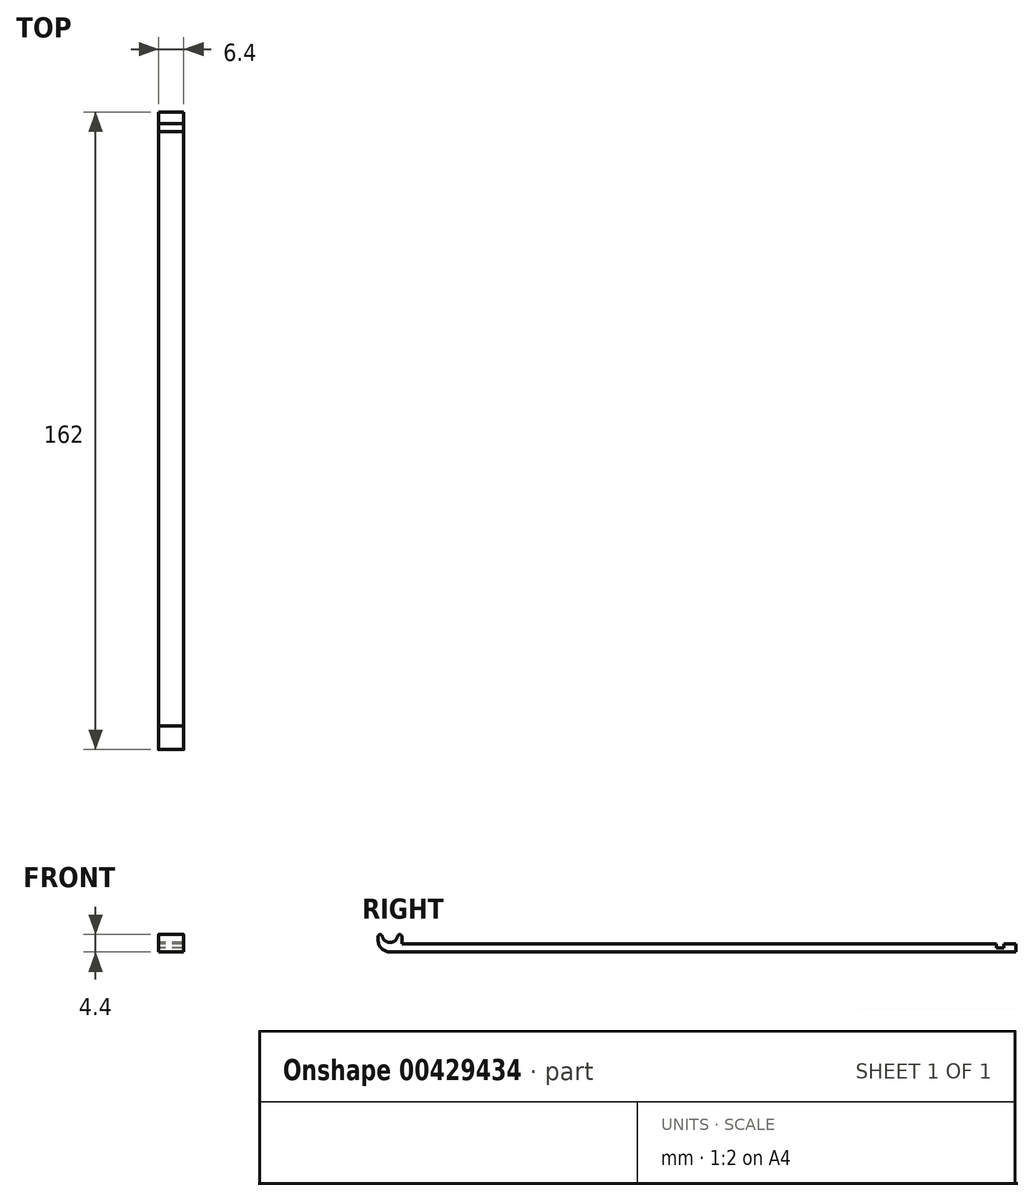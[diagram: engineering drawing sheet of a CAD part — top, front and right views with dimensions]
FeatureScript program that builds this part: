
annotation { "Feature Type Name" : "Feature", "Feature Type Description" : "" }
export const myFeature = defineFeature(function(context is Context, id is Id, definition is map)
    precondition{}
    {
        {
            var Q0;
            Q0=qCreatedBy(makeId("Right.planeOp"),FACE);
            var sketch = newSketch(context, id + "F0", { "sketchPlane" : qUnion([Q0])});
            skLineSegment(sketch, "E0.bottom", {"start": v(0, 0) * mm, "end": v(-159, 0) * mm});
            skLineSegment(sketch, "E0.top", {"start": v(0, 2) * mm, "end": v(-156, 2) * mm});
            skLineSegment(sketch, "E0.left", {"start": v(0, 0) * mm, "end": v(0, 2) * mm});
            skArc(sketch, "E1", {"start": v(-160.96, 4) * mm, "mid": v(-159, 2.4) * mm, "end": v(-157.04, 4) * mm});
            skLineSegment(sketch, "E2", {"start": v(-159, 4.4) * mm, "end": v(-157, 4.4) * mm, "construction": true});
            skLineSegment(sketch, "E3.top", {"start": v(-161.45, 4.4) * mm, "end": v(-161.5, 4.4) * mm});
            skLineSegment(sketch, "E3.right", {"start": v(-162, 3) * mm, "end": v(-162, 3.9) * mm});
            skLineSegment(sketch, "E4.bottom", {"start": v(-156.55, 4.4) * mm, "end": v(-156.5, 4.4) * mm});
            skLineSegment(sketch, "E4.right", {"start": v(-156, 3.9) * mm, "end": v(-156, 2) * mm});
            skPoint(sketch, "E5.start.orphan", {"position": v(-161, 4.4) * mm});
            skPoint(sketch, "E6.visualSharp", {"position": v(-162, 4.4) * mm});
            skArc(sketch, "E6.filletArc", {"start": v(-161.5, 4.4) * mm, "mid": v(-161.85, 4.25) * mm, "end": v(-162, 3.9) * mm});
            skPoint(sketch, "E7.visualSharp", {"position": v(-157, 4.4) * mm});
            skArc(sketch, "E7.filletArc", {"start": v(-156.55, 4.4) * mm, "mid": v(-156.87, 4.29) * mm, "end": v(-157.04, 4) * mm});
            skPoint(sketch, "E8.visualSharp", {"position": v(-156, 4.4) * mm});
            skArc(sketch, "E8.filletArc", {"start": v(-156, 3.9) * mm, "mid": v(-156.15, 4.25) * mm, "end": v(-156.5, 4.4) * mm});
            skArc(sketch, "E9.filletArc", {"start": v(-160.96, 4) * mm, "mid": v(-161.13, 4.29) * mm, "end": v(-161.45, 4.4) * mm});
            skPoint(sketch, "E10.visualSharp", {"position": v(-162, 0) * mm});
            skArc(sketch, "E10.filletArc", {"start": v(-162, 3) * mm, "mid": v(-161.12, 0.88) * mm, "end": v(-159, 0) * mm});
            skLineSegment(sketch, "E11.bottom", {"start": v(-5, 2) * mm, "end": v(-3, 2) * mm});
            skLineSegment(sketch, "E11.top", {"start": v(-5, 1) * mm, "end": v(-3, 1) * mm});
            skLineSegment(sketch, "E11.left", {"start": v(-5, 2) * mm, "end": v(-5, 1) * mm});
            skLineSegment(sketch, "E11.right", {"start": v(-3, 2) * mm, "end": v(-3, 1) * mm});
            skSolve(sketch);
        }
        {
            var Q0;
            Q0=makeQuery(id+"F0.imprint","IMPRINT",FACE,{"disambiguationData":[TD([[makeQuery(id+"F0.imprint","IMPRINT",EDGE,{"derivedFrom":sQuery(id+"F0.wireOp",EDGE,"E0.bottom")}),-1.0]])]});
            var Q1;
            {var subQ0=sQuery(id+"F0.wireOp",EDGE,"xZPfzYTH-SQou-s59R-LWdT-SighDjZiqHr3");Q1=makeQuery(id+"F0.imprint","IMPRINT",FACE,{"disambiguationData":[TD([[makeQuery(id+"F0.imprint","IMPRINT",EDGE,{"derivedFrom":subQ0}),-1.0]])]});}
            var Q2;
            {var subQ0=sQuery(id+"F0.wireOp",EDGE,"E1");var subQ1=sQuery(id+"F0.wireOp",EDGE,"E0.top");var subQ2=makeQuery(id+"F0.imprint","INTERSECT",VERTEX,{"disambiguationData":[OD(0.0)],"derivedFrom":[subQ1,subQ0]});Q2=makeQuery(id+"F0.imprint","IMPRINT",FACE,{"disambiguationData":[TD([[makeQuery(id+"F0.imprint","IMPRINT",EDGE,{"disambiguationData":[TD([[subQ2,-1.0]])],"derivedFrom":subQ1}),1.0]])]});}
            var Q3;
            {var subQ0=sQuery(id+"F0.wireOp",EDGE,"E1");var subQ1=sQuery(id+"F0.wireOp",EDGE,"E0.top");var subQ2=makeQuery(id+"F0.imprint","INTERSECT",VERTEX,{"disambiguationData":[OD(0.0)],"derivedFrom":[subQ1,subQ0]});Q3=makeQuery(id+"F0.imprint","IMPRINT",FACE,{"disambiguationData":[TD([[makeQuery(id+"F0.imprint","IMPRINT",EDGE,{"disambiguationData":[TD([[subQ2,-1.0]])],"derivedFrom":subQ1}),-1.0]])]});}
            var Q4;
            {var subQ0=sQuery(id+"F0.wireOp",EDGE,"E5");Q4=makeQuery(id+"F0.imprint","IMPRINT",FACE,{"disambiguationData":[TD([[makeQuery(id+"F0.imprint","IMPRINT",EDGE,{"derivedFrom":subQ0}),1.0]])]});}
            extrude(context, id + "F1", {"entities" : qUnion([Q0, Q1, Q2, Q3, Q4]), "depth" : 6.4 * mm});
        }
    });
